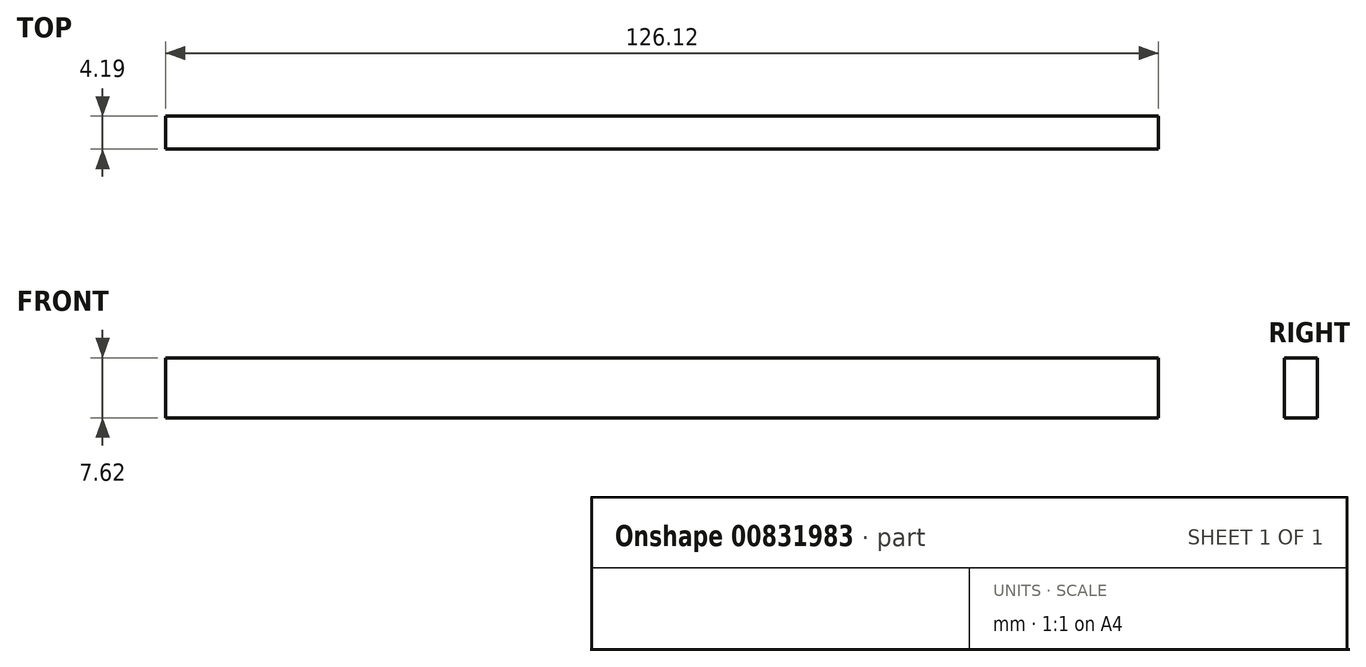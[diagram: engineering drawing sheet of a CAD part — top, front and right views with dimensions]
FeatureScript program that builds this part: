
annotation { "Feature Type Name" : "Feature", "Feature Type Description" : "" }
export const myFeature = defineFeature(function(context is Context, id is Id, definition is map)
    precondition{}
    {
        {
            var Q0;
            Q0=qCreatedBy(makeId("Top.planeOp"),FACE);
            var sketch = newSketch(context, id + "F0", { "sketchPlane" : qUnion([Q0])});
            skLineSegment(sketch, "E0.bottom", {"start": v(-65.34, 11.2) * mm, "end": v(60.78, 11.2) * mm});
            skLineSegment(sketch, "E0.top", {"start": v(-65.34, -0.27) * mm, "end": v(60.78, -0.27) * mm});
            skLineSegment(sketch, "E0.left", {"start": v(-65.34, 11.2) * mm, "end": v(-65.34, -0.27) * mm});
            skLineSegment(sketch, "E0.right", {"start": v(60.78, 11.2) * mm, "end": v(60.78, -0.27) * mm});
            skLineSegment(sketch, "E1.bottom", {"start": v(-65.34, 7.56) * mm, "end": v(60.78, 7.56) * mm});
            skLineSegment(sketch, "E1.top", {"start": v(-65.34, 3.92) * mm, "end": v(60.78, 3.92) * mm});
            skLineSegment(sketch, "E1.left", {"start": v(-65.34, 7.56) * mm, "end": v(-65.34, 3.92) * mm});
            skLineSegment(sketch, "E1.right", {"start": v(60.78, 7.56) * mm, "end": v(60.78, 3.92) * mm});
            skSolve(sketch);
        }
        {
            var Q0;
            {var subQ0=sQuery(id+"F0.wireOp",EDGE,"E0.top");Q0=makeQuery(id+"F0.imprint","IMPRINT",FACE,{"disambiguationData":[TD([[makeQuery(id+"F0.imprint","IMPRINT",EDGE,{"derivedFrom":subQ0}),1.0]])]});}
            extrude(context, id + "F1", {"entities" : qUnion([Q0]), "depth" : 7.62 * mm, "offsetDistance" : 25.4 * mm});
        }
    });
